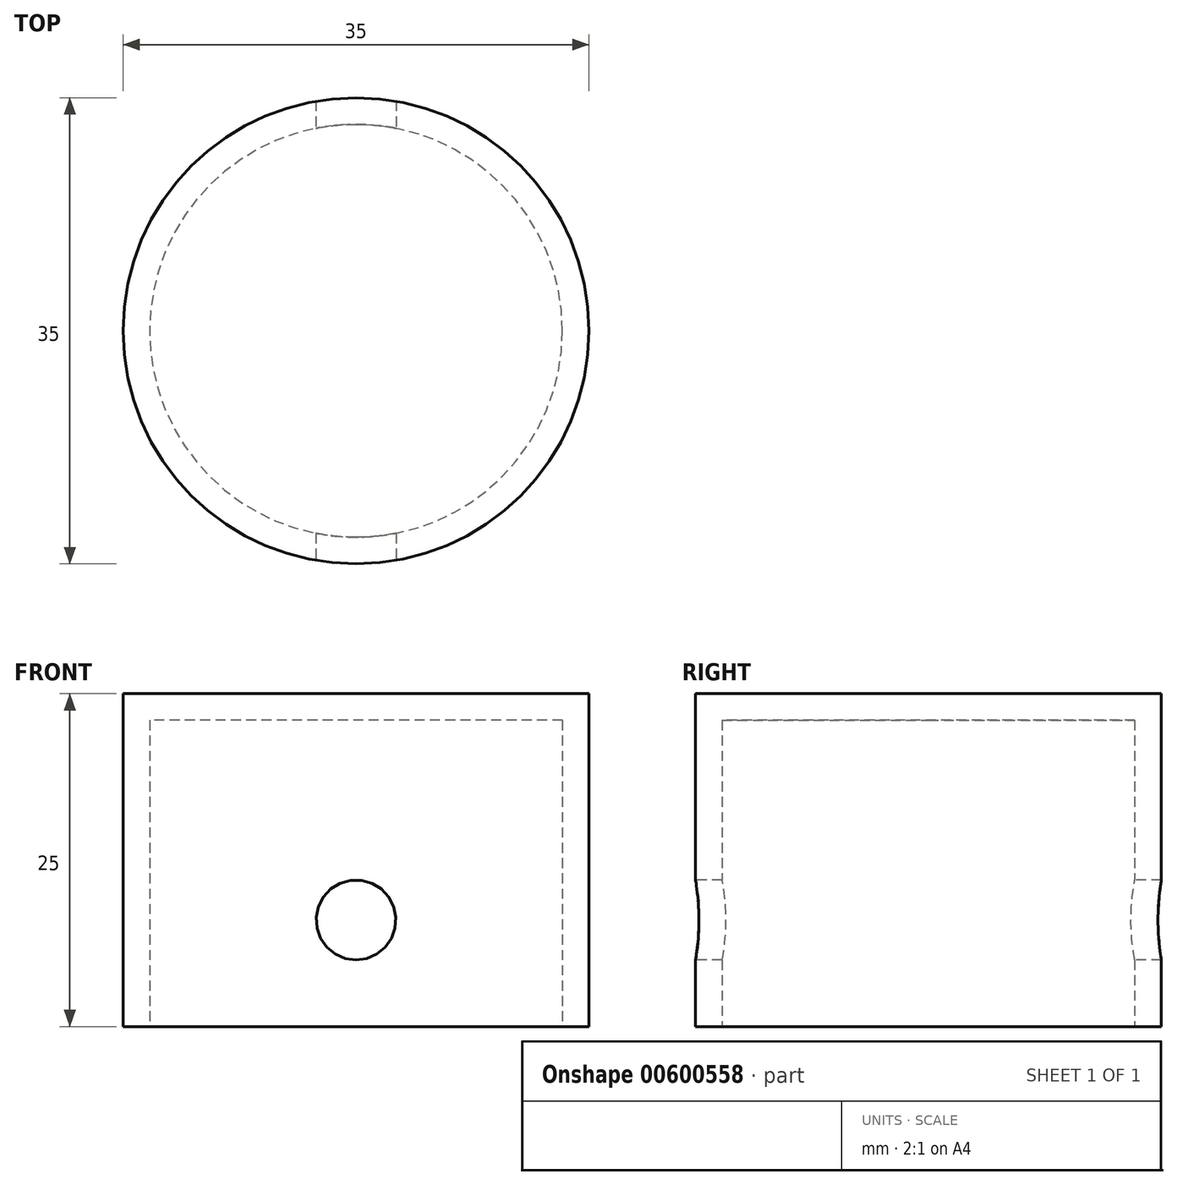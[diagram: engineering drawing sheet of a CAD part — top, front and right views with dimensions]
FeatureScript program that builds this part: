
annotation { "Feature Type Name" : "Feature", "Feature Type Description" : "" }
export const myFeature = defineFeature(function(context is Context, id is Id, definition is map)
    precondition{}
    {
        {
            var Q0;
            Q0=qCreatedBy(makeId("Top.planeOp"),FACE);
            var sketch = newSketch(context, id + "F0", { "sketchPlane" : qUnion([Q0])});
            skCircle(sketch, "E0", {"center": v(0, 0) * mm, "radius": 17.5 * mm});
            skSolve(sketch);
        }
        {
            var Q0;
            Q0 = qSketchRegion(id + "F0", true);
            extrude(context, id + "F1", {"entities" : qUnion([Q0]), "depth" : 25 * mm, "offsetDistance" : 25 * mm});
        }
        {
            var Q0;
            Q0=makeQuery(id+"F1.opExtrude","CAP_FACE",FACE,{"disambiguationData":[OSD([sQuery(id+"F0.wireOp",EDGE,"E0")])],"isStart":true});
            shell(context, id + "F2", {"entities" : qUnion([Q0]), "thickness" : 2 * mm});
        }
        {
            var Q0;
            Q0=qCreatedBy(makeId("Front.planeOp"),FACE);
            var sketch = newSketch(context, id + "F3", { "sketchPlane" : qUnion([Q0])});
            skCircle(sketch, "E1", {"center": v(0, 8) * mm, "radius": 3 * mm});
            skSolve(sketch);
        }
        {
            var Q0;
            Q0 = qSketchRegion(id + "F3", true);
            extrude(context, id + "F4", {"entities" : qUnion([Q0]), "operationType" : NewBodyOperationType.REMOVE, "endBound" : BoundingType.SYMMETRIC, "oppositeDirection" : true, "depth" : 39.2 * mm, "offsetDistance" : 25 * mm});
        }
    });
